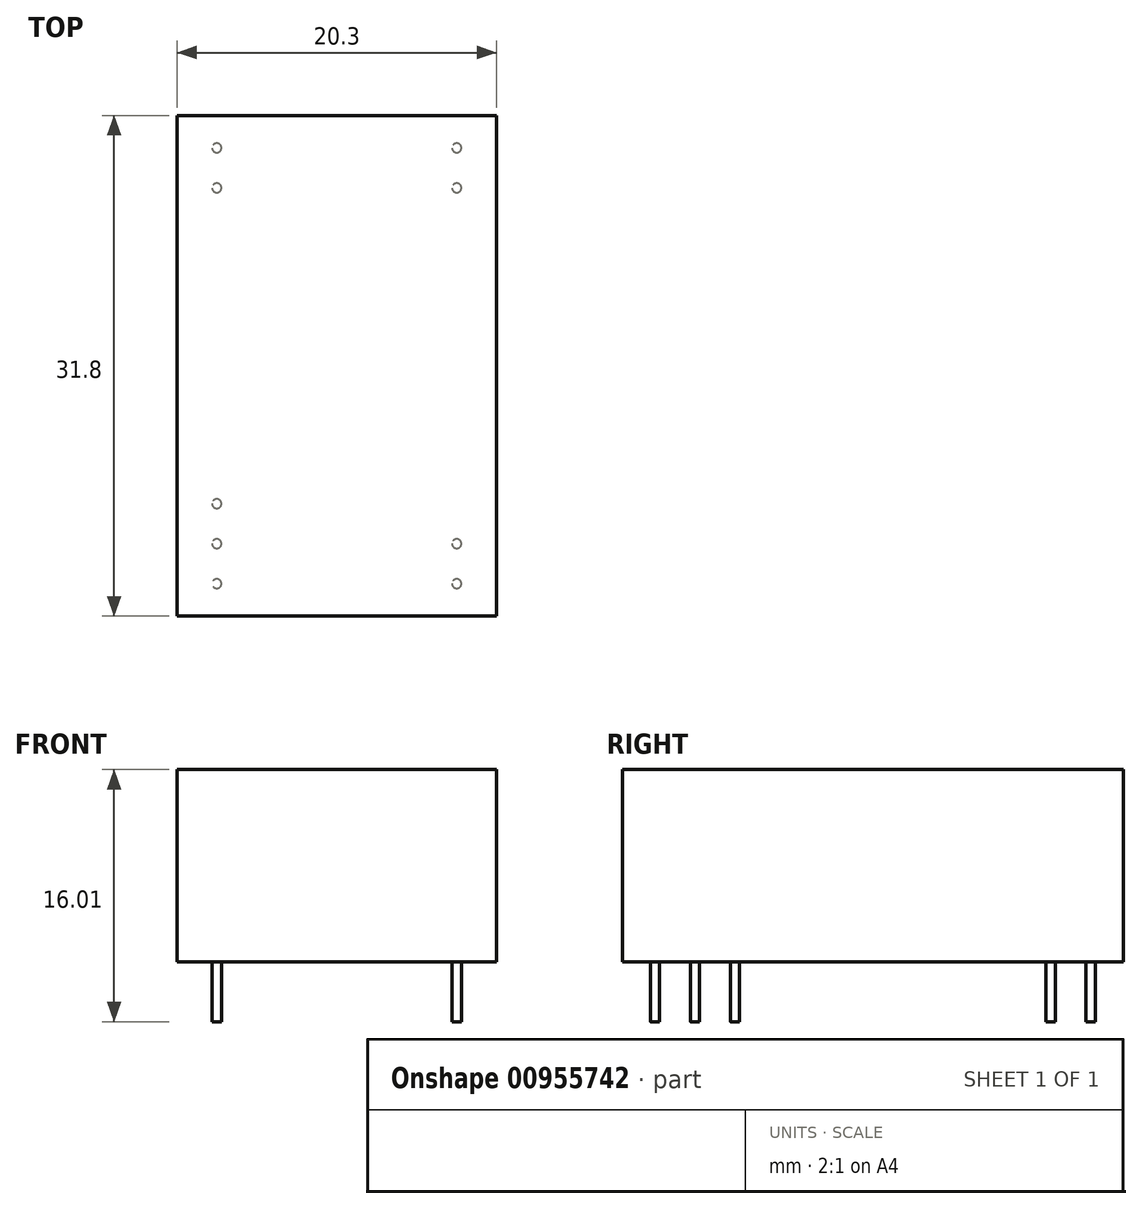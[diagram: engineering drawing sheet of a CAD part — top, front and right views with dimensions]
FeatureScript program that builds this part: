
annotation { "Feature Type Name" : "Feature", "Feature Type Description" : "" }
export const myFeature = defineFeature(function(context is Context, id is Id, definition is map)
    precondition{}
    {
        {
            var Q0;
            Q0=qCreatedBy(makeId("Top.planeOp"),FACE);
            var sketch = newSketch(context, id + "F0", { "sketchPlane" : qUnion([Q0])});
            skLineSegment(sketch, "E0.bottom", {"start": v(0, 0) * mm, "end": v(20.3, 0) * mm});
            skLineSegment(sketch, "E0.top", {"start": v(0, -31.8) * mm, "end": v(20.3, -31.8) * mm});
            skLineSegment(sketch, "E0.left", {"start": v(0, 0) * mm, "end": v(0, -31.8) * mm});
            skLineSegment(sketch, "E0.right", {"start": v(20.3, 0) * mm, "end": v(20.3, -31.8) * mm});
            skSolve(sketch);
        }
        {
            var Q0;
            Q0=makeQuery(id+"F0.imprint","IMPRINT",FACE,{"disambiguationData":[TD([[makeQuery(id+"F0.imprint","IMPRINT",EDGE,{"derivedFrom":sQuery(id+"F0.wireOp",EDGE,"E0.bottom")}),-1.0]])]});
            extrude(context, id + "F1", {"entities" : qUnion([Q0]), "depth" : 12.2 * mm, "offsetDistance" : 25 * mm});
        }
        {
            var Q0;
            Q0=makeQuery(id+"F1.opExtrude","CAP_FACE",FACE,{"disambiguationData":[OSD([sQuery(id+"F0.wireOp",EDGE,"E0.bottom"),sQuery(id+"F0.wireOp",EDGE,"E0.top"),sQuery(id+"F0.wireOp",EDGE,"E0.left"),sQuery(id+"F0.wireOp",EDGE,"E0.right")])],"isStart":true});
            var sketch = newSketch(context, id + "F2", { "sketchPlane" : qUnion([Q0])});
            skPoint(sketch, "E1", {"position": v(2.53, 29.74) * mm});
            skPoint(sketch, "E2", {"position": v(2.53, 27.2) * mm});
            skPoint(sketch, "E3", {"position": v(2.53, 24.66) * mm});
            skPoint(sketch, "E4", {"position": v(2.53, 4.6) * mm});
            skPoint(sketch, "E5", {"position": v(2.53, 2.06) * mm});
            skPoint(sketch, "E6", {"position": v(17.77, 2.06) * mm});
            skPoint(sketch, "E7", {"position": v(17.77, 4.6) * mm});
            skPoint(sketch, "E8", {"position": v(17.77, 29.74) * mm});
            skPoint(sketch, "E9", {"position": v(17.77, 27.2) * mm});
            skLineSegment(sketch, "E10", {"start": v(2.53, 29.74) * mm, "end": v(17.77, 29.74) * mm});
            skPoint(sketch, "E11", {"position": v(10.15, 29.74) * mm});
            skPoint(sketch, "E12", {"position": v(10.15, 31.8) * mm});
            skCircle(sketch, "E13", {"center": v(2.53, 29.74) * mm, "radius": 0.3 * mm});
            skCircle(sketch, "E14", {"center": v(2.53, 27.2) * mm, "radius": 0.3 * mm});
            skCircle(sketch, "E15", {"center": v(2.53, 24.66) * mm, "radius": 0.3 * mm});
            skCircle(sketch, "E16", {"center": v(2.53, 4.6) * mm, "radius": 0.3 * mm});
            skCircle(sketch, "E17", {"center": v(2.53, 2.06) * mm, "radius": 0.3 * mm});
            skCircle(sketch, "E18", {"center": v(17.77, 2.06) * mm, "radius": 0.3 * mm});
            skCircle(sketch, "E19", {"center": v(17.77, 4.6) * mm, "radius": 0.3 * mm});
            skCircle(sketch, "E20", {"center": v(17.77, 27.2) * mm, "radius": 0.3 * mm});
            skCircle(sketch, "E21", {"center": v(17.77, 29.74) * mm, "radius": 0.3 * mm});
            skSolve(sketch);
        }
        {
            var Q0;
            Q0=makeQuery(id+"F2.imprint","IMPRINT",FACE,{"disambiguationData":[TD([[makeQuery(id+"F2.imprint","IMPRINT",EDGE,{"derivedFrom":sQuery(id+"F2.wireOp",EDGE,"E13")}),1.0]])]});
            var Q1;
            Q1=makeQuery(id+"F2.imprint","IMPRINT",FACE,{"disambiguationData":[TD([[makeQuery(id+"F2.imprint","IMPRINT",EDGE,{"derivedFrom":sQuery(id+"F2.wireOp",EDGE,"E14")}),1.0]])]});
            var Q2;
            Q2=makeQuery(id+"F2.imprint","IMPRINT",FACE,{"disambiguationData":[TD([[makeQuery(id+"F2.imprint","IMPRINT",EDGE,{"derivedFrom":sQuery(id+"F2.wireOp",EDGE,"E15")}),1.0]])]});
            var Q3;
            Q3=makeQuery(id+"F2.imprint","IMPRINT",FACE,{"disambiguationData":[TD([[makeQuery(id+"F2.imprint","IMPRINT",EDGE,{"derivedFrom":sQuery(id+"F2.wireOp",EDGE,"E21")}),1.0]])]});
            var Q4;
            Q4=makeQuery(id+"F2.imprint","IMPRINT",FACE,{"disambiguationData":[TD([[makeQuery(id+"F2.imprint","IMPRINT",EDGE,{"derivedFrom":sQuery(id+"F2.wireOp",EDGE,"E20")}),1.0]])]});
            var Q5;
            Q5=makeQuery(id+"F2.imprint","IMPRINT",FACE,{"disambiguationData":[TD([[makeQuery(id+"F2.imprint","IMPRINT",EDGE,{"derivedFrom":sQuery(id+"F2.wireOp",EDGE,"E19")}),1.0]])]});
            var Q6;
            Q6=makeQuery(id+"F2.imprint","IMPRINT",FACE,{"disambiguationData":[TD([[makeQuery(id+"F2.imprint","IMPRINT",EDGE,{"derivedFrom":sQuery(id+"F2.wireOp",EDGE,"E18")}),1.0]])]});
            var Q7;
            Q7=makeQuery(id+"F2.imprint","IMPRINT",FACE,{"disambiguationData":[TD([[makeQuery(id+"F2.imprint","IMPRINT",EDGE,{"derivedFrom":sQuery(id+"F2.wireOp",EDGE,"E17")}),1.0]])]});
            var Q8;
            Q8=makeQuery(id+"F2.imprint","IMPRINT",FACE,{"disambiguationData":[TD([[makeQuery(id+"F2.imprint","IMPRINT",EDGE,{"derivedFrom":sQuery(id+"F2.wireOp",EDGE,"E16")}),1.0]])]});
            extrude(context, id + "F3", {"entities" : qUnion([Q0, Q1, Q2, Q3, Q4, Q5, Q6, Q7, Q8]), "operationType" : NewBodyOperationType.ADD, "depth" : 3.81 * mm, "offsetDistance" : 25 * mm});
        }
    });
